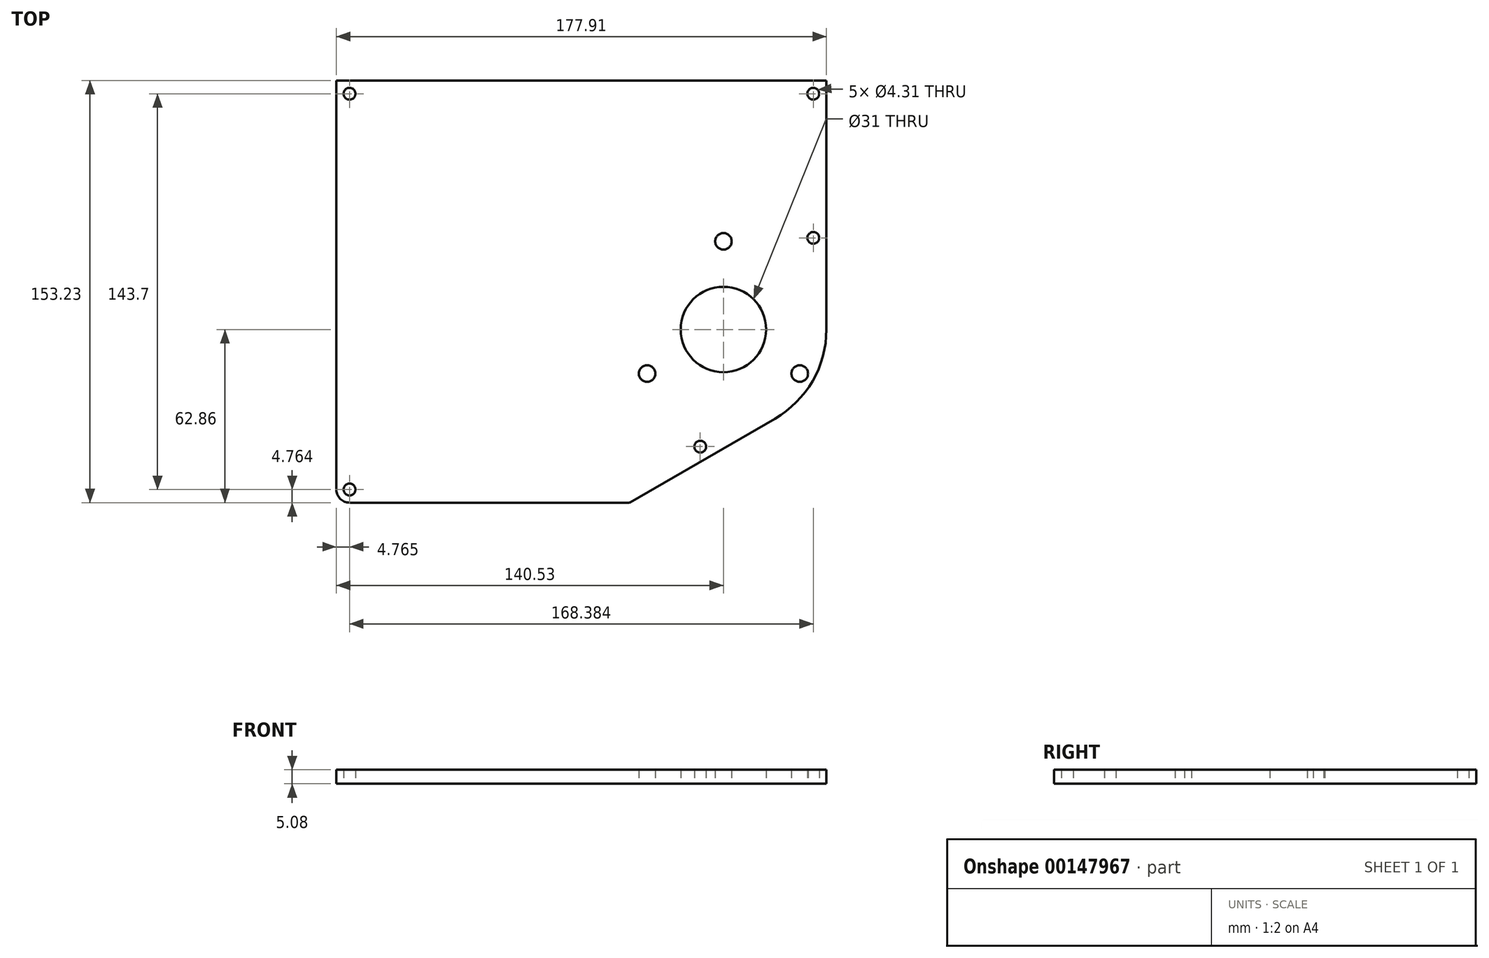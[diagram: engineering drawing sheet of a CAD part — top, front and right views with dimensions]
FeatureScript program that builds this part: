
annotation { "Feature Type Name" : "Feature", "Feature Type Description" : "" }
export const myFeature = defineFeature(function(context is Context, id is Id, definition is map)
    precondition{}
    {
        {
            var Q0;
            Q0=qCreatedBy(makeId("Top.planeOp"),FACE);
            var sketch = newSketch(context, id + "F0", { "sketchPlane" : qUnion([Q0])});
            skLineSegment(sketch, "E0", {"start": v(0, 0) * mm, "end": v(0, 32) * mm, "construction": true});
            skLineSegment(sketch, "E1", {"start": v(0, 0) * mm, "end": v(27.71, -16) * mm, "construction": true});
            skLineSegment(sketch, "E2", {"start": v(0, 0) * mm, "end": v(-27.71, -16) * mm, "construction": true});
            skLineSegment(sketch, "E3", {"start": v(0, 32) * mm, "end": v(27.71, -16) * mm, "construction": true});
            skLineSegment(sketch, "E4", {"start": v(27.71, -16) * mm, "end": v(-27.71, -16) * mm, "construction": true});
            skLineSegment(sketch, "E5", {"start": v(-27.71, -16) * mm, "end": v(0, 32) * mm, "construction": true});
            skCircle(sketch, "E6", {"center": v(0, 0) * mm, "radius": 15.5 * mm});
            skCircle(sketch, "E7", {"center": v(0, 32) * mm, "radius": 3 * mm});
            skCircle(sketch, "E8", {"center": v(-27.71, -16) * mm, "radius": 3 * mm});
            skCircle(sketch, "E9", {"center": v(27.71, -16) * mm, "radius": 3 * mm});
            skLineSegment(sketch, "E10.bottom", {"start": v(-140.53, 90.37) * mm, "end": v(37.38, 90.37) * mm});
            skLineSegment(sketch, "E10.right", {"start": v(37.38, 90.37) * mm, "end": v(37.38, 0) * mm});
            skLineSegment(sketch, "E11", {"start": v(37.38, 85.6) * mm, "end": v(32.62, 85.6) * mm, "construction": true});
            skLineSegment(sketch, "E12", {"start": v(32.62, 85.6) * mm, "end": v(32.62, 90.37) * mm, "construction": true});
            skCircle(sketch, "E13", {"center": v(32.62, 85.6) * mm, "radius": 2.15 * mm});
            skLineSegment(sketch, "E14", {"start": v(-140.53, 90.37) * mm, "end": v(-140.53, -62.86) * mm});
            skLineSegment(sketch, "E15", {"start": v(32.62, 85.6) * mm, "end": v(-135.77, 85.6) * mm, "construction": true});
            skCircle(sketch, "E16", {"center": v(-135.77, 85.6) * mm, "radius": 2.15 * mm});
            skCircle(sketch, "E17", {"center": v(-8.42, -42.52) * mm, "radius": 4.76 * mm, "construction": true});
            skCircle(sketch, "E18", {"center": v(32.62, 33.28) * mm, "radius": 2.15 * mm});
            skCircle(sketch, "E19", {"center": v(-8.42, -42.52) * mm, "radius": 2.15 * mm});
            skLineSegment(sketch, "E20", {"start": v(0, 0) * mm, "end": v(-34.11, 0) * mm, "construction": true});
            skLineSegment(sketch, "E21", {"start": v(-34.11, 0) * mm, "end": v(-34.11, -62.86) * mm, "construction": true});
            skArc(sketch, "E22", {"start": v(18.7, -32.37) * mm, "mid": v(32.37, -18.7) * mm, "end": v(37.38, 0) * mm});
            skLineSegment(sketch, "E23", {"start": v(18.7, -32.37) * mm, "end": v(-34.11, -62.86) * mm});
            skLineSegment(sketch, "E24", {"start": v(-34.11, -62.86) * mm, "end": v(-140.53, -62.86) * mm});
            skLineSegment(sketch, "E25", {"start": v(-135.77, 85.6) * mm, "end": v(-135.77, -58.1) * mm, "construction": true});
            skLineSegment(sketch, "E26", {"start": v(-135.77, -58.1) * mm, "end": v(-135.77, -62.86) * mm, "construction": true});
            skLineSegment(sketch, "E27", {"start": v(-135.77, -58.1) * mm, "end": v(-140.53, -58.1) * mm, "construction": true});
            skCircle(sketch, "E28", {"center": v(27.71, -16) * mm, "radius": 5.38 * mm, "construction": true});
            skCircle(sketch, "E29", {"center": v(0, 0) * mm, "radius": 37 * mm, "construction": true});
            skCircle(sketch, "E30", {"center": v(-8.42, -42.52) * mm, "radius": 6.35 * mm, "construction": true});
            skLineSegment(sketch, "E31", {"start": v(37.38, 0) * mm, "end": v(32.62, 0) * mm, "construction": true});
            skLineSegment(sketch, "E32", {"start": v(32.62, 0) * mm, "end": v(32.62, 33.28) * mm, "construction": true});
            skCircle(sketch, "E33", {"center": v(-135.77, -58.1) * mm, "radius": 2.15 * mm});
            skSolve(sketch);
        }
        {
            var Q0;
            Q0=qSketchRegion(id+"F0",true);
            extrude(context, id + "F1", {"entities" : qUnion([Q0]), "depth" : 5.08 * mm});
        }
        {
            var Q0;
            Q0=makeQuery(id+"F1.opExtrude","SWEPT_EDGE",EDGE,{"disambiguationData":[OSD([sQuery(id+"F0.wireOp",EDGE,"E14"),sQuery(id+"F0.wireOp",EDGE,"E24")])]});
            fillet(context, id + "F2", {"entities" : qUnion([Q0]), "radius" : 4.76 * mm, "tangentPropagation" : true, "allowEdgeOverflow" : false});
        }
        {
            var Q0;
            Q0=makeQuery(id+"F1.opExtrude","SWEPT_EDGE",EDGE,{"disambiguationData":[OSD([sQuery(id+"F0.wireOp",EDGE,"E23"),sQuery(id+"F0.wireOp",EDGE,"E24")])]});
            fillet(context, id + "F3", {"entities" : qUnion([Q0]), "radius" : 0.76 * mm, "tangentPropagation" : true, "allowEdgeOverflow" : false});
        }
    });
